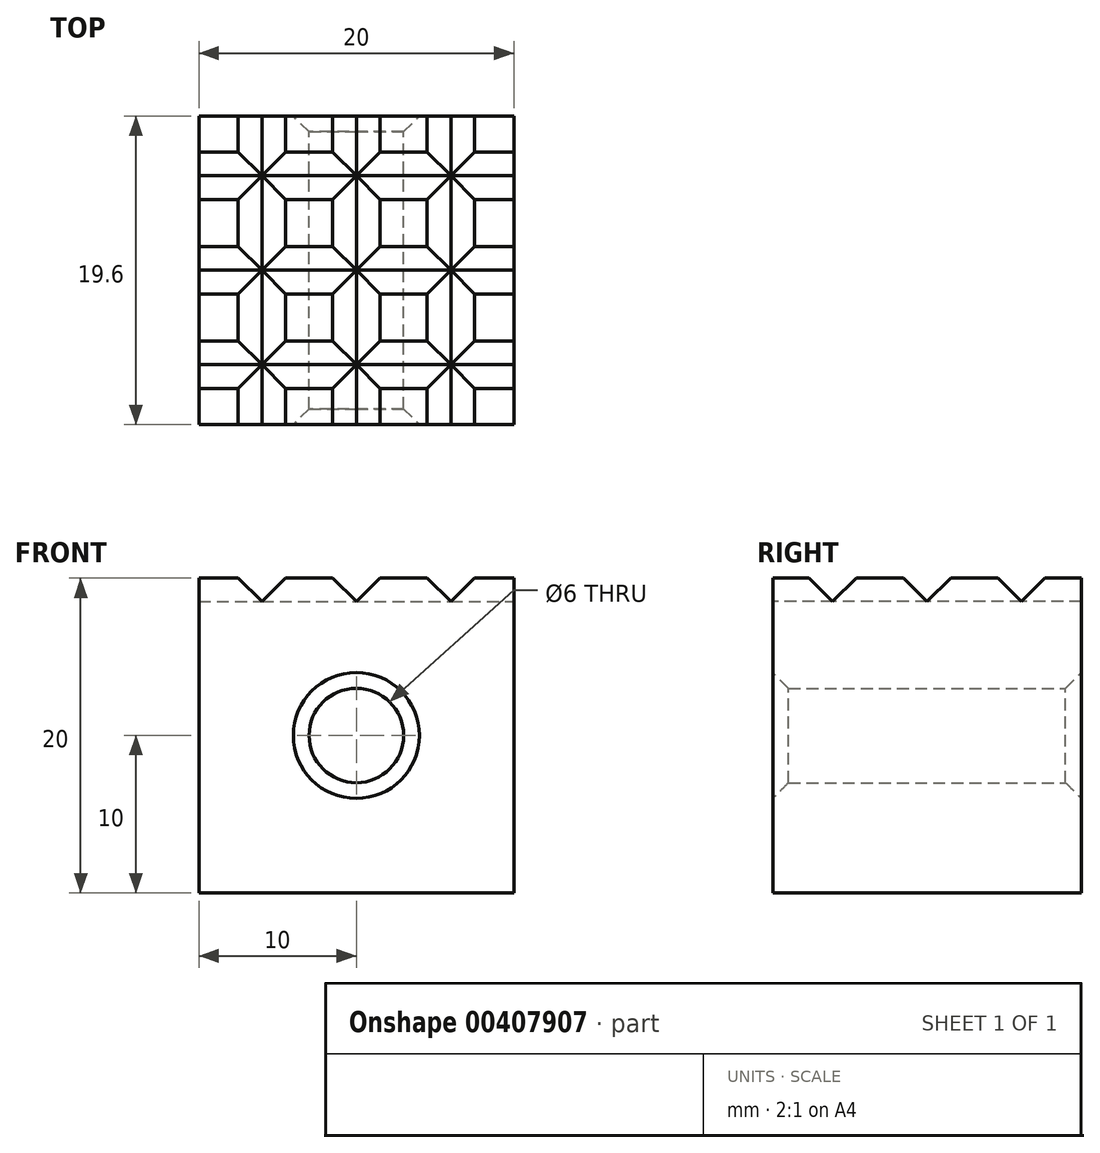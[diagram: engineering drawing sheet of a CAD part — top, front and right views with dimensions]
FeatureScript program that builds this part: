
annotation { "Feature Type Name" : "Feature", "Feature Type Description" : "" }
export const myFeature = defineFeature(function(context is Context, id is Id, definition is map)
    precondition{}
    {
        {
            var Q0;
            Q0=qCreatedBy(makeId("Front.planeOp"),FACE);
            var sketch = newSketch(context, id + "F0", { "sketchPlane" : qUnion([Q0])});
            skLineSegment(sketch, "E0.bottom", {"start": v(10, -10) * mm, "end": v(-10, -10) * mm});
            skLineSegment(sketch, "E0.top", {"start": v(10, 10) * mm, "end": v(-10, 10) * mm});
            skLineSegment(sketch, "E0.left", {"start": v(10, -10) * mm, "end": v(10, 10) * mm});
            skLineSegment(sketch, "E0.right", {"start": v(-10, -10) * mm, "end": v(-10, 10) * mm});
            skPoint(sketch, "E0.middle", {"position": v(0, 0) * mm});
            skCircle(sketch, "E1", {"center": v(0, 0) * mm, "radius": 3 * mm});
            skSolve(sketch);
        }
        {
            var Q0;
            Q0 = qSketchRegion(id + "F0", true);
            extrude(context, id + "F1", {"entities" : qUnion([Q0]), "depth" : 19.6 * mm});
        }
        {
            var Q0;
            Q0=makeQuery(id+"F1.opExtrude","CAP_EDGE",EDGE,{"disambiguationData":[OSD([sQuery(id+"F0.wireOp",EDGE,"E1")])],"isStart":false});
            var Q1;
            Q1=makeQuery(id+"F1.opExtrude","CAP_EDGE",EDGE,{"disambiguationData":[OSD([sQuery(id+"F0.wireOp",EDGE,"E1")])],"isStart":true});
            chamfer(context, id + "F2", {"entities" : qUnion([Q0, Q1]), "width" : 1 * mm, "tangentPropagation" : true});
        }
        {
            var Q0;
            Q0=makeQuery(id+"F1.opExtrude","CAP_FACE",FACE,{"disambiguationData":[OSD([sQuery(id+"F0.wireOp",EDGE,"E0.bottom"),sQuery(id+"F0.wireOp",EDGE,"E0.top"),sQuery(id+"F0.wireOp",EDGE,"E0.left"),sQuery(id+"F0.wireOp",EDGE,"E0.right"),sQuery(id+"F0.wireOp",EDGE,"E1")])],"isStart":false});
            var sketch = newSketch(context, id + "F3", { "sketchPlane" : qUnion([Q0])});
            skLineSegment(sketch, "E2", {"start": v(-7.5, 10) * mm, "end": v(-6, 8.5) * mm});
            skLineSegment(sketch, "E3", {"start": v(-6, 8.5) * mm, "end": v(-4.5, 10) * mm});
            skLineSegment(sketch, "E4", {"start": v(-4.5, 10) * mm, "end": v(-7.5, 10) * mm});
            skLineSegment(sketch, "E5.1.0.0", {"start": v(-1.5, 10) * mm, "end": v(0, 8.5) * mm});
            skLineSegment(sketch, "E5.1.0.1", {"start": v(0, 8.5) * mm, "end": v(1.5, 10) * mm});
            skLineSegment(sketch, "E5.1.0.2", {"start": v(1.5, 10) * mm, "end": v(-1.5, 10) * mm});
            skLineSegment(sketch, "E5.2.0.0", {"start": v(4.5, 10) * mm, "end": v(6, 8.5) * mm});
            skLineSegment(sketch, "E5.2.0.1", {"start": v(6, 8.5) * mm, "end": v(7.5, 10) * mm});
            skLineSegment(sketch, "E5.2.0.2", {"start": v(7.5, 10) * mm, "end": v(4.5, 10) * mm});
            skLineSegment(sketch, "E5.direction1", {"start": v(-6, 8.5) * mm, "end": v(0, 8.5) * mm, "construction": true});
            skSolve(sketch);
        }
        {
            var Q0;
            Q0=makeQuery(id+"F3.imprint","IMPRINT",FACE,{"disambiguationData":[TD([[makeQuery(id+"F3.imprint","IMPRINT",EDGE,{"derivedFrom":sQuery(id+"F3.wireOp",EDGE,"E2")}),1.0]])]});
            var Q1;
            Q1=makeQuery(id+"F3.imprint","IMPRINT",FACE,{"disambiguationData":[TD([[makeQuery(id+"F3.imprint","IMPRINT",EDGE,{"derivedFrom":sQuery(id+"F3.wireOp",EDGE,"E5.1.0.0")}),1.0]])]});
            var Q2;
            Q2=makeQuery(id+"F3.imprint","IMPRINT",FACE,{"disambiguationData":[TD([[makeQuery(id+"F3.imprint","IMPRINT",EDGE,{"derivedFrom":sQuery(id+"F3.wireOp",EDGE,"E5.2.0.0")}),1.0]])]});
            extrude(context, id + "F4", {"entities" : qUnion([Q0, Q1, Q2]), "operationType" : NewBodyOperationType.REMOVE, "endBound" : BoundingType.THROUGH_ALL, "oppositeDirection" : true, "depth" : 25 * mm});
        }
        {
            var Q0;
            Q0=makeQuery(id+"F1.opExtrude","SWEPT_FACE",FACE,{"disambiguationData":[OSD([sQuery(id+"F0.wireOp",EDGE,"E0.left")])]});
            var sketch = newSketch(context, id + "F5", { "sketchPlane" : qUnion([Q0])});
            skLineSegment(sketch, "E6", {"start": v(-17.3, 10) * mm, "end": v(-14.3, 10) * mm});
            skLineSegment(sketch, "E7", {"start": v(-14.3, 10) * mm, "end": v(-15.8, 8.5) * mm});
            skLineSegment(sketch, "E8", {"start": v(-15.8, 8.5) * mm, "end": v(-17.3, 10) * mm});
            skLineSegment(sketch, "E9.1.0.0", {"start": v(-9.8, 8.5) * mm, "end": v(-11.3, 10) * mm});
            skLineSegment(sketch, "E9.1.0.1", {"start": v(-11.3, 10) * mm, "end": v(-8.3, 10) * mm});
            skLineSegment(sketch, "E9.1.0.2", {"start": v(-8.3, 10) * mm, "end": v(-9.8, 8.5) * mm});
            skLineSegment(sketch, "E9.2.0.0", {"start": v(-3.8, 8.5) * mm, "end": v(-5.3, 10) * mm});
            skLineSegment(sketch, "E9.2.0.1", {"start": v(-5.3, 10) * mm, "end": v(-2.3, 10) * mm});
            skLineSegment(sketch, "E9.2.0.2", {"start": v(-2.3, 10) * mm, "end": v(-3.8, 8.5) * mm});
            skLineSegment(sketch, "E9.direction1", {"start": v(-15.8, 8.5) * mm, "end": v(-9.8, 8.5) * mm, "construction": true});
            skSolve(sketch);
        }
        {
            var Q0;
            Q0=makeQuery(id+"F5.imprint","IMPRINT",FACE,{"disambiguationData":[TD([[makeQuery(id+"F5.imprint","IMPRINT",EDGE,{"derivedFrom":sQuery(id+"F5.wireOp",EDGE,"E6")}),-1.0]])]});
            var Q1;
            Q1=makeQuery(id+"F5.imprint","IMPRINT",FACE,{"disambiguationData":[TD([[makeQuery(id+"F5.imprint","IMPRINT",EDGE,{"derivedFrom":sQuery(id+"F5.wireOp",EDGE,"E9.1.0.0")}),-1.0]])]});
            var Q2;
            Q2=makeQuery(id+"F5.imprint","IMPRINT",FACE,{"disambiguationData":[TD([[makeQuery(id+"F5.imprint","IMPRINT",EDGE,{"derivedFrom":sQuery(id+"F5.wireOp",EDGE,"E9.2.0.0")}),-1.0]])]});
            extrude(context, id + "F6", {"entities" : qUnion([Q0, Q1, Q2]), "operationType" : NewBodyOperationType.REMOVE, "endBound" : BoundingType.THROUGH_ALL, "oppositeDirection" : true, "depth" : 25 * mm});
        }
    });
